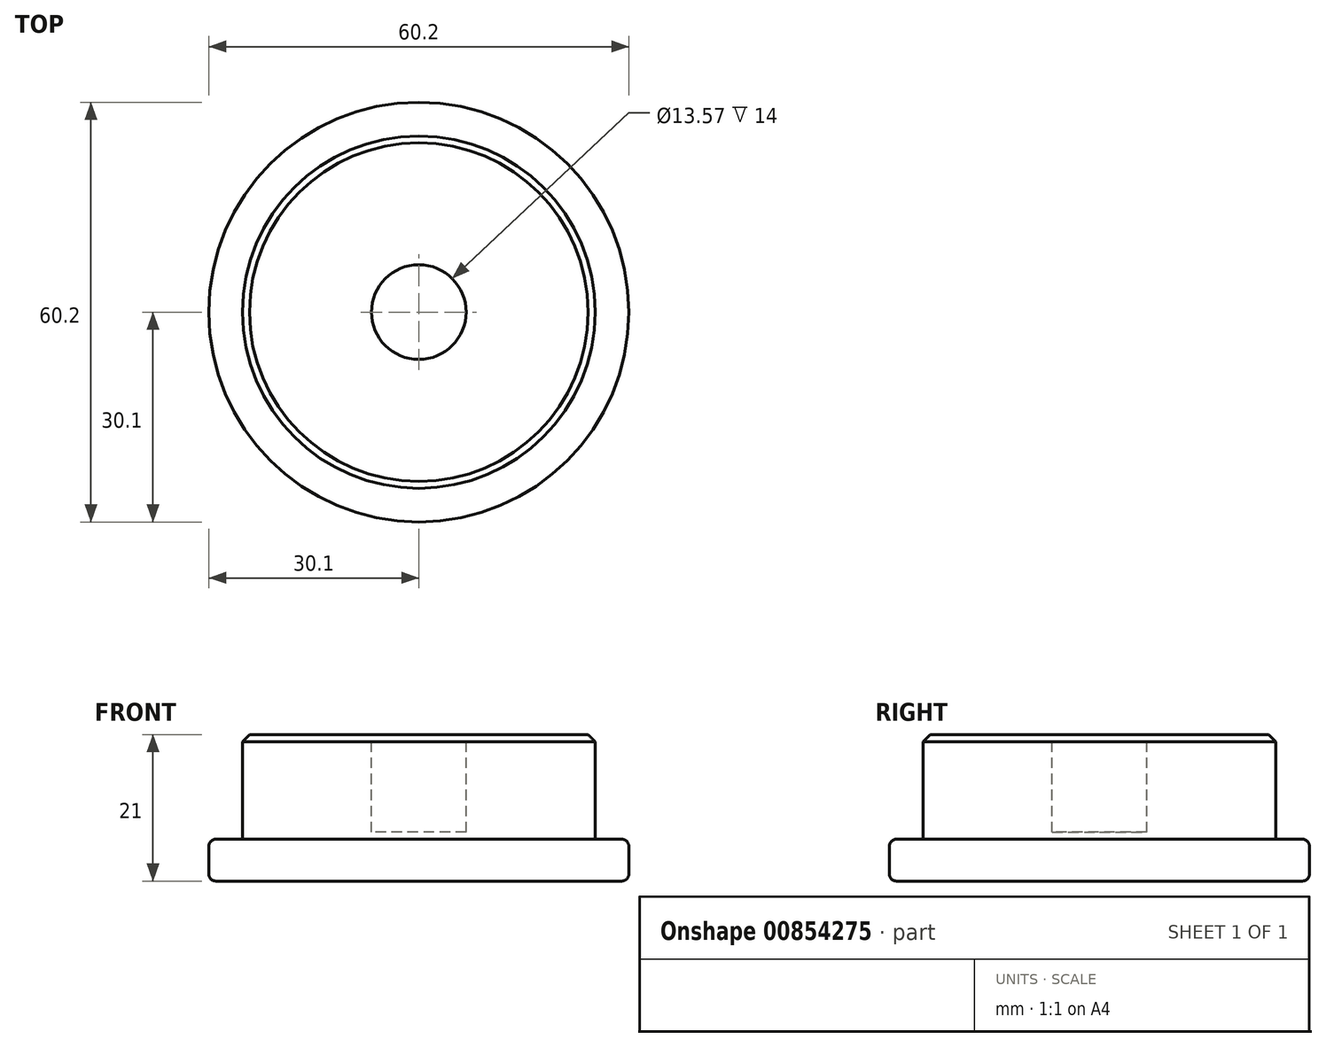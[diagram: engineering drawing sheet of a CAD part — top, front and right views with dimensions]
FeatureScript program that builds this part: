
annotation { "Feature Type Name" : "Feature", "Feature Type Description" : "" }
export const myFeature = defineFeature(function(context is Context, id is Id, definition is map)
    precondition{}
    {
        {
            var Q0;
            Q0=qCreatedBy(makeId("Top.planeOp"),FACE);
            var sketch = newSketch(context, id + "F0", { "sketchPlane" : qUnion([Q0])});
            skCircle(sketch, "E0", {"center": v(0, 0) * mm, "radius": 30.1 * mm});
            skSolve(sketch);
        }
        {
            var Q0;
            Q0 = qSketchRegion(id + "F0", true);
            extrude(context, id + "F1", {"entities" : qUnion([Q0]), "depth" : 6 * mm, "offsetDistance" : 25 * mm});
        }
        {
            var Q0;
            Q0=makeQuery(id+"F1.opExtrude","CAP_FACE",FACE,{"disambiguationData":[OSD([sQuery(id+"F0.wireOp",EDGE,"E0")])],"isStart":false});
            var sketch = newSketch(context, id + "F2", { "sketchPlane" : qUnion([Q0])});
            skCircle(sketch, "E1", {"center": v(0, 0) * mm, "radius": 25.27 * mm});
            skSolve(sketch);
        }
        {
            var Q0;
            Q0=makeQuery(id+"F2.imprint","IMPRINT",FACE,{"disambiguationData":[TD([[makeQuery(id+"F2.imprint","IMPRINT",EDGE,{"derivedFrom":sQuery(id+"F2.wireOp",EDGE,"E1")}),1.0]])]});
            extrude(context, id + "F3", {"entities" : qUnion([Q0]), "operationType" : NewBodyOperationType.ADD, "depth" : 15 * mm, "offsetDistance" : 25 * mm});
        }
        {
            var Q0;
            Q0=makeQuery(id+"F3.opExtrude","CAP_FACE",FACE,{"disambiguationData":[OSD([sQuery(id+"F2.wireOp",EDGE,"E1")])],"isStart":false});
            var sketch = newSketch(context, id + "F4", { "sketchPlane" : qUnion([Q0])});
            skCircle(sketch, "E2", {"center": v(0, 0) * mm, "radius": 6.79 * mm});
            skSolve(sketch);
        }
        {
            var Q0;
            Q0 = qSketchRegion(id + "F4", true);
            extrude(context, id + "F5", {"entities" : qUnion([Q0]), "operationType" : NewBodyOperationType.REMOVE, "oppositeDirection" : true, "depth" : 14 * mm, "offsetDistance" : 25 * mm});
        }
        {
            var Q0;
            Q0=makeQuery(id+"F1.opExtrude","CAP_EDGE",EDGE,{"disambiguationData":[OSD([sQuery(id+"F0.wireOp",EDGE,"E0")])],"isStart":false});
            fillet(context, id + "F6", {"entities" : qUnion([Q0]), "radius" : 1 * mm, "tangentPropagation" : true, "allowEdgeOverflow" : false});
        }
        {
            var Q0;
            Q0=makeQuery(id+"F1.opExtrude","CAP_EDGE",EDGE,{"disambiguationData":[OSD([sQuery(id+"F0.wireOp",EDGE,"E0")])],"isStart":true});
            fillet(context, id + "F7", {"entities" : qUnion([Q0]), "radius" : 1 * mm, "tangentPropagation" : true, "allowEdgeOverflow" : false});
        }
        {
            var Q0;
            Q0=makeQuery(id+"F3.opExtrude","CAP_EDGE",EDGE,{"disambiguationData":[OSD([sQuery(id+"F2.wireOp",EDGE,"E1")])],"isStart":false});
            chamfer(context, id + "F8", {"entities" : qUnion([Q0]), "width" : 1 * mm, "tangentPropagation" : true});
        }
    });
